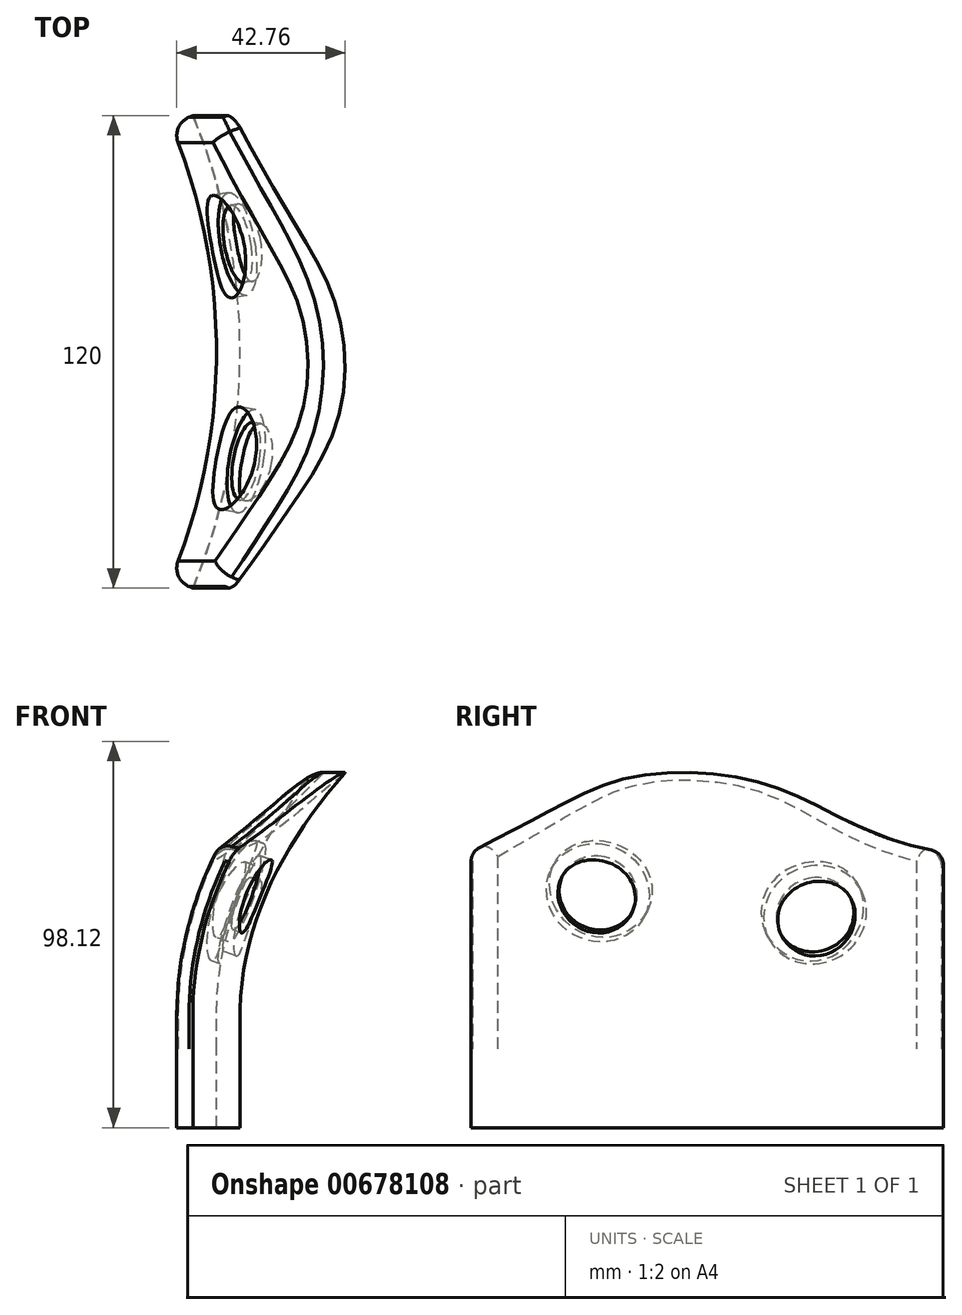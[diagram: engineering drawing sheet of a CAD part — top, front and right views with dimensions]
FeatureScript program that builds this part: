
annotation { "Feature Type Name" : "Feature", "Feature Type Description" : "" }
export const myFeature = defineFeature(function(context is Context, id is Id, definition is map)
    precondition{}
    {
        {
            var Q0;
            Q0=qCreatedBy(makeId("Top.planeOp"),FACE);
            var sketch = newSketch(context, id + "F0", { "sketchPlane" : qUnion([Q0])});
            skCircle(sketch, "E0", {"center": v(0, 0) * mm, "radius": 150 * mm});
            skCircle(sketch, "E1", {"center": v(0, 0) * mm, "radius": 156 * mm});
            skLineSegment(sketch, "E2", {"start": v(0, 0) * mm, "end": v(144, 60) * mm});
            skLineSegment(sketch, "E3", {"start": v(0, 0) * mm, "end": v(144, -60) * mm});
            skLineSegment(sketch, "E4", {"start": v(144, -60) * mm, "end": v(144, 60) * mm, "construction": true});
            skPoint(sketch, "E5", {"position": v(150, 0) * mm});
            skLineSegment(sketch, "E6", {"start": v(0, 0) * mm, "end": v(194.97, 0) * mm, "construction": true});
            skPoint(sketch, "E6.endSnap0", {"position": v(144, 0) * mm});
            skLineSegment(sketch, "E7", {"start": v(0, 0) * mm, "end": v(292.01, 51.49) * mm, "construction": true});
            skLineSegment(sketch, "E8", {"start": v(0, 0) * mm, "end": v(281.75, -49.68) * mm, "construction": true});
            skLineSegment(sketch, "E9", {"start": v(0, 0) * mm, "end": v(17.6, 99.8) * mm, "construction": true});
            skLineSegment(sketch, "E10", {"start": v(0, 0) * mm, "end": v(-17.8, 101) * mm, "construction": true});
            skSolve(sketch);
        }
        {
            var Q0;
            Q0=qCreatedBy(makeId("Front.planeOp"),FACE);
            var sketch = newSketch(context, id + "F1", { "sketchPlane" : qUnion([Q0])});
            skLineSegment(sketch, "E11.0", {"start": v(-150, 0) * mm, "end": v(150, 0) * mm, "construction": true});
            skLineSegment(sketch, "E12.0", {"start": v(-156, 0) * mm, "end": v(156, 0) * mm, "construction": true});
            skPoint(sketch, "E13.0", {"position": v(144, 0) * mm});
            skLineSegment(sketch, "E14", {"start": v(150, 0) * mm, "end": v(156, 0) * mm, "construction": true});
            skPoint(sketch, "E15", {"position": v(153, 0) * mm});
            skFitSpline(sketch, "E16", {"points": [v(153, 0) * mm, v(153, 6.97) * mm, v(183, 75) * mm], "startDerivative": vector(0, 39.39) * mm, "endDerivative": vector(117.55, 127) * mm});
            skLineSegment(sketch, "E17", {"start": v(153, 0) * mm, "end": v(153, 85.18) * mm, "construction": true});
            skLineSegment(sketch, "E18", {"start": v(0, 0) * mm, "end": v(0, 132.16) * mm, "construction": true});
            skLineSegment(sketch, "E19", {"start": v(159.74, 40.26) * mm, "end": v(-10.19, 118.1) * mm, "construction": true});
            skLineSegment(sketch, "E20", {"start": v(0, 0) * mm, "end": v(39.97, 112.88) * mm, "construction": true});
            skSolve(sketch);
        }
        {
            var Q0;
            {var subQ0=sQuery(id+"F0.wireOp",EDGE,"E2");var subQ1=sQuery(id+"F0.wireOp",EDGE,"E0");var subQ2=makeQuery(id+"F0.imprint","INTERSECT",VERTEX,{"derivedFrom":[subQ1,subQ0]});Q0=makeQuery(id+"F0.imprint","IMPRINT",FACE,{"disambiguationData":[TD([[makeQuery(id+"F0.imprint","IMPRINT",EDGE,{"disambiguationData":[TD([[subQ2,1.0]])],"derivedFrom":subQ1}),-1.0]])]});}
            var Q1;
            Q1=sQuery(id+"F1.wireOp",EDGE,"E16");
            sweep(context, id + "F2", {"profiles" : qUnion([Q0]), "path" : qUnion([Q1])});
        }
        {
            var Q0;
            Q0=makeQuery(id+"F2.opSweep","SWEPT_EDGE",EDGE,{"disambiguationData":[OSD([sQuery(id+"F0.wireOp",EDGE,"E1"),sQuery(id+"F0.wireOp",EDGE,"E3"),sQuery(id+"F1.wireOp",EDGE,"E16")])]});
            cPoint(context, id + "F3", {"entities" : qUnion([Q0]), "parameter" : 0.5});
        }
        {
            var Q0;
            Q0=qCreatedBy(makeId("Front.planeOp"),FACE);
            var Q1;
            Q1=qCreatedBy(id+"F3",VERTEX);
            cPlane(context, id + "F4", {"entities" : qUnion([Q0, Q1]), "cplaneType" : CPlaneType.PLANE_POINT, "offset" : 25 * mm, "width" : 150 * mm, "height" : 150 * mm});
        }
        {
            var Q0;
            Q0=qCreatedBy(id+"F4.planeOp",FACE);
            var sketch = newSketch(context, id + "F5", { "sketchPlane" : qUnion([Q0])});
            skLineSegment(sketch, "E21", {"start": v(16.14, 50) * mm, "end": v(342.74, 50) * mm});
            skLineSegment(sketch, "E22.top", {"start": v(16.14, 200) * mm, "end": v(342.74, 200) * mm});
            skLineSegment(sketch, "E22.left", {"start": v(16.14, 50) * mm, "end": v(16.14, 200) * mm});
            skLineSegment(sketch, "E22.right", {"start": v(342.74, 50) * mm, "end": v(342.74, 200) * mm});
            skSolve(sketch);
        }
        {
            var Q0;
            Q0=qCreatedBy(makeId("Right.planeOp"),FACE);
            var sketch = newSketch(context, id + "F6", { "sketchPlane" : qUnion([Q0])});
            skPoint(sketch, "E23.0", {"position": v(-60, 50) * mm});
            skLineSegment(sketch, "E24", {"start": v(-74, 50) * mm, "end": v(-141.5, 50) * mm, "construction": true});
            skFitSpline(sketch, "E25.0", {"points": [v(60, 0) * mm, v(1000, 60) * mm, v(35.14, 1000) * mm, v(60, 64.87) * mm, v(1000, 60) * mm, v(84.32, 1000) * mm, v(60, 86.04) * mm, v(1000, 60) * mm, v(89.63, 1000) * mm, v(60, 91.5) * mm, v(1000, 60) * mm, v(95.4, 1000) * mm, v(60, 97.44) * mm, v(1000, 60) * mm, v(101.6, 1000) * mm, v(60, 103.7) * mm, v(1000, 60) * mm, v(107.93, 1000) * mm], "construction": true});
            skFitSpline(sketch, "E26.0", {"points": [v(-60, 0) * mm, v(1000, -60) * mm, v(35.14, 1000) * mm, v(-60, 64.87) * mm, v(1000, -60) * mm, v(84.32, 1000) * mm, v(-60, 86.04) * mm, v(1000, -60) * mm, v(89.63, 1000) * mm, v(-60, 91.5) * mm, v(1000, -60) * mm, v(95.4, 1000) * mm, v(-60, 97.44) * mm, v(1000, -60) * mm, v(101.6, 1000) * mm, v(-60, 103.7) * mm, v(1000, -60) * mm, v(107.93, 1000) * mm], "construction": true});
            skLineSegment(sketch, "E27", {"start": v(68.45, 50) * mm, "end": v(-5.43, 50) * mm, "construction": true});
            skLineSegment(sketch, "E28", {"start": v(28.07, 70) * mm, "end": v(-24.08, 70) * mm, "construction": true});
            skFitSpline(sketch, "E29", {"points": [v(60, 50) * mm, v(21.87, 64.69) * mm, v(0, 70) * mm, v(-21.64, 68.5) * mm, v(-60, 50) * mm], "startDerivative": vector(-172.17, 24.2) * mm, "endDerivative": vector(-217.51, -110.98) * mm});
            skSolve(sketch);
        }
        {
            var Q0;
            Q0=makeQuery(id+"F5.imprint","IMPRINT",FACE,{"disambiguationData":[TD([[makeQuery(id+"F5.imprint","IMPRINT",EDGE,{"derivedFrom":sQuery(id+"F5.wireOp",EDGE,"E21")}),1.0]])]});
            var Q1;
            Q1=sQuery(id+"F6.wireOp",EDGE,"E29");
            sweep(context, id + "F7", {"operationType" : NewBodyOperationType.REMOVE, "profiles" : qUnion([Q0]), "path" : qUnion([Q1]), "keepProfileOrientation" : true});
        }
        {
            var Q0;
            Q0=makeQuery(id+"F7.boolean.opBoolean","INTERSECT",EDGE,{"derivedFrom":[makeQuery(id+"F2.opSweep","SWEPT_FACE",FACE,{"disambiguationData":[OSD([sQuery(id+"F0.wireOp",EDGE,"E0"),sQuery(id+"F1.wireOp",EDGE,"E16")])]}),makeQuery(id+"F7.opSweep","SWEPT_FACE",FACE,{"disambiguationData":[OSD([sQuery(id+"F5.wireOp",EDGE,"E21"),sQuery(id+"F6.wireOp",EDGE,"E29")])]})]});
            fillet(context, id + "F8", {"entities" : qUnion([Q0]), "radius" : 5 * mm, "tangentPropagation" : true, "allowEdgeOverflow" : false});
        }
        {
            var Q0;
            Q0=makeQuery(id+"F2.opSweep","SWEPT_EDGE",EDGE,{"disambiguationData":[OSD([sQuery(id+"F0.wireOp",EDGE,"E0"),sQuery(id+"F0.wireOp",EDGE,"E2"),sQuery(id+"F1.wireOp",EDGE,"E16")])]});
            var Q1;
            Q1=makeQuery(id+"F2.opSweep","SWEPT_EDGE",EDGE,{"disambiguationData":[OSD([sQuery(id+"F0.wireOp",EDGE,"E0"),sQuery(id+"F0.wireOp",EDGE,"E3"),sQuery(id+"F1.wireOp",EDGE,"E16")])]});
            fillet(context, id + "F9", {"entities" : qUnion([Q0, Q1]), "radius" : 5 * mm, "tangentPropagation" : true, "allowEdgeOverflow" : false});
        }
        {
            var Q0;
            Q0=makeQuery(id+"F2.opSweep","CAP_FACE",FACE,{"disambiguationData":[OSD([sQuery(id+"F0.wireOp",EDGE,"E0"),sQuery(id+"F0.wireOp",EDGE,"E1"),sQuery(id+"F0.wireOp",EDGE,"E2"),sQuery(id+"F0.wireOp",EDGE,"E3"),sQuery(id+"F1.wireOp",VERTEX,"E16.start")])],"isStart":true});
            var sketch = newSketch(context, id + "F10", { "sketchPlane" : qUnion([Q0])});
            skLineSegment(sketch, "E30.0.0", {"start": v(144, 60) * mm, "end": v(143, 59.58) * mm});
            skArc(sketch, "E30.0.1", {"start": v(143, 59.58) * mm, "mid": v(140.33, 56.95) * mm, "end": v(140.25, 53.2) * mm});
            skArc(sketch, "E30.0.2", {"start": v(140.25, -53.2) * mm, "mid": v(150, 0) * mm, "end": v(140.25, 53.2) * mm});
            skArc(sketch, "E30.0.3", {"start": v(140.25, -53.2) * mm, "mid": v(140.33, -56.95) * mm, "end": v(143, -59.58) * mm});
            skLineSegment(sketch, "E30.0.4", {"start": v(144, -60) * mm, "end": v(143, -59.58) * mm});
            skArc(sketch, "E30.0.5", {"start": v(144, -60) * mm, "mid": v(156, 0) * mm, "end": v(144, 60) * mm});
            skSolve(sketch);
        }
        {
            var Q0;
            Q0=makeQuery(id+"F10.imprint","IMPRINT",FACE,{"disambiguationData":[TD([[makeQuery(id+"F10.imprint","IMPRINT",EDGE,{"derivedFrom":sQuery(id+"F10.wireOp",EDGE,"E30.0.0")}),-1.0]])]});
            extrude(context, id + "F11", {"entities" : qUnion([Q0]), "operationType" : NewBodyOperationType.ADD, "depth" : 20 * mm, "offsetDistance" : 25 * mm});
        }
        {
            var Q0;
            Q0=sQuery(id+"F1.wireOp",EDGE,"E12.0");
            cPoint(context, id + "F12", {"entities" : qUnion([Q0]), "parameter" : 0.5});
        }
        {
            var Q0;
            Q0=sQuery(id+"F0.wireOp",VERTEX,"E10.end");
            var Q1;
            Q1 = qCreatedBy(id + "F12" ,VERTEX);
            var Q2;
            Q2=sQuery(id+"F1.wireOp",VERTEX,"E20.end");
            cPlane(context, id + "F13", {"entities" : qUnion([Q0, Q1, Q2]), "cplaneType" : CPlaneType.THREE_POINT, "offset" : 25 * mm, "width" : 150 * mm, "height" : 150 * mm});
        }
        {
            var Q0;
            Q0=qCreatedBy(id+"F13.planeOp",FACE);
            var sketch = newSketch(context, id + "F14", { "sketchPlane" : qUnion([Q0])});
            skCircle(sketch, "E31", {"center": v(4.88, 84) * mm, "radius": 10 * mm});
            skCircle(sketch, "E32", {"center": v(4.88, 84) * mm, "radius": 13.25 * mm});
            skLineSegment(sketch, "E33.0", {"start": v(0, 0) * mm, "end": v(5.66, 97.48) * mm, "construction": true});
            skSolve(sketch);
        }
        {
            var Q0;
            Q0=makeQuery(id+"F14.imprint","IMPRINT",FACE,{"disambiguationData":[TD([[makeQuery(id+"F14.imprint","IMPRINT",EDGE,{"derivedFrom":sQuery(id+"F14.wireOp",EDGE,"E31")}),1.0]])]});
            var Q1;
            Q1=makeQuery(id+"F2.opSweep","SWEPT_BODY",BODY,{"disambiguationData":[OSD([sQuery(id+"F0.wireOp",EDGE,"E0"),sQuery(id+"F0.wireOp",EDGE,"E1"),sQuery(id+"F0.wireOp",EDGE,"E2"),sQuery(id+"F0.wireOp",EDGE,"E3"),sQuery(id+"F1.wireOp",EDGE,"E16")])]});
            extrude(context, id + "F15", {"entities" : qUnion([Q0]), "operationType" : NewBodyOperationType.REMOVE, "endBound" : BoundingType.UP_TO_BODY, "depth" : 25 * mm, "endBoundEntityBody" : qUnion([Q1]), "hasOffset" : true, "offsetDistance" : 10 * mm, "offsetOppositeDirection" : true});
        }
        {
            var Q0;
            Q0=makeQuery(id+"F14.imprint","IMPRINT",FACE,{"disambiguationData":[TD([[makeQuery(id+"F14.imprint","IMPRINT",EDGE,{"derivedFrom":sQuery(id+"F14.wireOp",EDGE,"E31")}),-1.0]])]});
            extrude(context, id + "F16", {"entities" : qUnion([Q0]), "operationType" : NewBodyOperationType.REMOVE, "depth" : (133.7 + 4) * mm, "offsetDistance" : 25 * mm});
        }
        {
            var Q0;
            Q0=sQuery(id+"F0.wireOp",VERTEX,"E2.start");
            var Q1;
            Q1=sQuery(id+"F0.wireOp",VERTEX,"E9.end");
            var Q2;
            Q2=sQuery(id+"F1.wireOp",VERTEX,"E20.end");
            cPlane(context, id + "F17", {"entities" : qUnion([Q0, Q1, Q2]), "cplaneType" : CPlaneType.THREE_POINT, "offset" : 25 * mm, "width" : 150 * mm, "height" : 150 * mm});
        }
        {
            var Q0;
            Q0=qCreatedBy(id+"F17.planeOp",FACE);
            var sketch = newSketch(context, id + "F18", { "sketchPlane" : qUnion([Q0])});
            skLineSegment(sketch, "E34.0", {"start": v(0, 0) * mm, "end": v(5.46, 94.05) * mm, "construction": true});
            skCircle(sketch, "E35", {"center": v(5.23, 90) * mm, "radius": 10 * mm});
            skCircle(sketch, "E36", {"center": v(5.23, 90) * mm, "radius": 13.25 * mm});
            skSolve(sketch);
        }
        {
            var Q0;
            Q0=makeQuery(id+"F18.imprint","IMPRINT",FACE,{"disambiguationData":[TD([[makeQuery(id+"F18.imprint","IMPRINT",EDGE,{"derivedFrom":sQuery(id+"F18.wireOp",EDGE,"E35")}),1.0]])]});
            var Q1;
            Q1=makeQuery(id+"F2.opSweep","SWEPT_BODY",BODY,{"disambiguationData":[OSD([sQuery(id+"F0.wireOp",EDGE,"E0"),sQuery(id+"F0.wireOp",EDGE,"E1"),sQuery(id+"F0.wireOp",EDGE,"E2"),sQuery(id+"F0.wireOp",EDGE,"E3"),sQuery(id+"F1.wireOp",EDGE,"E16")])]});
            extrude(context, id + "F19", {"entities" : qUnion([Q0]), "operationType" : NewBodyOperationType.REMOVE, "endBound" : BoundingType.UP_TO_BODY, "oppositeDirection" : true, "depth" : 25 * mm, "endBoundEntityBody" : qUnion([Q1]), "hasOffset" : true, "offsetDistance" : 10 * mm, "offsetOppositeDirection" : true});
        }
        {
            var Q0;
            Q0=makeQuery(id+"F18.imprint","IMPRINT",FACE,{"disambiguationData":[TD([[makeQuery(id+"F18.imprint","IMPRINT",EDGE,{"derivedFrom":sQuery(id+"F18.wireOp",EDGE,"E35")}),-1.0]])]});
            extrude(context, id + "F20", {"entities" : qUnion([Q0]), "operationType" : NewBodyOperationType.REMOVE, "oppositeDirection" : true, "depth" : (134 + 4) * mm, "offsetDistance" : 25 * mm});
        }
    });
